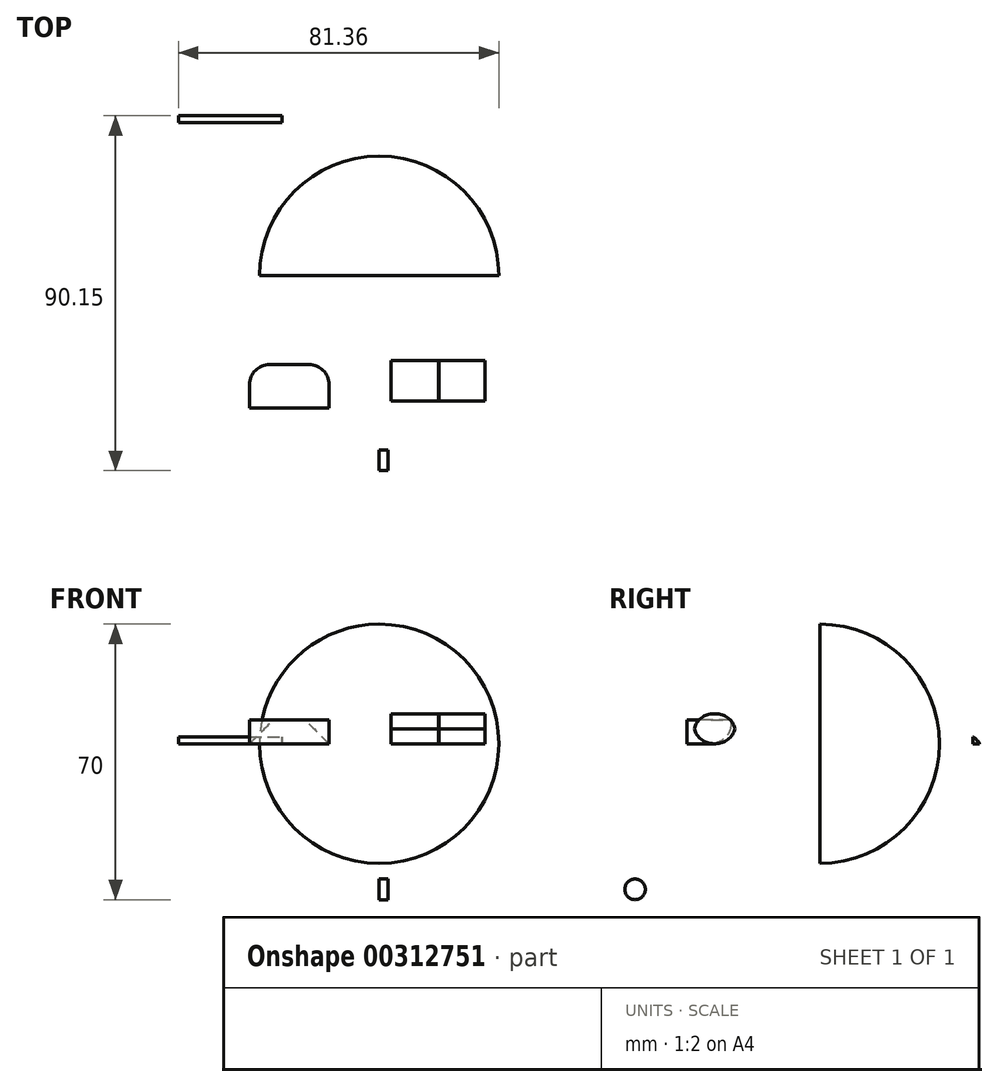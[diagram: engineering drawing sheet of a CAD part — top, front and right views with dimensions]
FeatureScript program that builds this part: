
annotation { "Feature Type Name" : "Feature", "Feature Type Description" : "" }
export const myFeature = defineFeature(function(context is Context, id is Id, definition is map)
    precondition{}
    {
        {
            var Q0;
            Q0=qCreatedBy(makeId("Front.planeOp"),FACE);
            var sketch = newSketch(context, id + "F0", { "sketchPlane" : qUnion([Q0])});
            skCircle(sketch, "E0", {"center": v(0, 0) * mm, "radius": 30.38 * mm});
            skLineSegment(sketch, "E1", {"start": v(0, 0) * mm, "end": v(30.38, 0) * mm});
            skLineSegment(sketch, "E2", {"start": v(30.38, 0) * mm, "end": v(-30.38, 0) * mm});
            skSolve(sketch);
        }
        {
            var Q0;
            {var subQ0=sQuery(id+"F0.wireOp",EDGE,"E2");var subQ4=makeQuery(id+"F0.imprint","IMPRINT",VERTEX,{"derivedFrom":subQ0});Q0=makeQuery(id+"F0.imprint","IMPRINT",FACE,{"disambiguationData":[TD([[makeQuery(id+"F0.imprint","IMPRINT",EDGE,{"disambiguationData":[TD([[subQ4,1.0]])],"derivedFrom":subQ0}),-1.0]])]});}
            var Q1;
            Q1=sQuery(id+"F0.wireOp",EDGE,"E2");
            revolve(context, id + "F1", {"entities" : qUnion([Q0]), "axis" : qUnion([Q1]), "revolveType" : RevolveType.ONE_DIRECTION, "angle" : 180 * degree});
        }
        {
            var Q0;
            Q0=qCreatedBy(makeId("Top.planeOp"),FACE);
            var sketch = newSketch(context, id + "F2", { "sketchPlane" : qUnion([Q0])});
            skLineSegment(sketch, "E3.bottom", {"start": v(26.83, -21.37) * mm, "end": v(15.2, -21.37) * mm});
            skLineSegment(sketch, "E3.top", {"start": v(26.83, -32.04) * mm, "end": v(15.2, -32.04) * mm});
            skLineSegment(sketch, "E3.left", {"start": v(26.83, -21.37) * mm, "end": v(26.83, -32.04) * mm});
            skLineSegment(sketch, "E3.right", {"start": v(15.2, -21.37) * mm, "end": v(15.2, -32.04) * mm});
            skLineSegment(sketch, "E4.bottom", {"start": v(15.04, -21.37) * mm, "end": v(2.99, -21.37) * mm});
            skLineSegment(sketch, "E4.top", {"start": v(15.04, -32.04) * mm, "end": v(2.99, -32.04) * mm});
            skLineSegment(sketch, "E4.left", {"start": v(15.04, -21.37) * mm, "end": v(15.04, -32.04) * mm});
            skLineSegment(sketch, "E4.right", {"start": v(2.99, -21.37) * mm, "end": v(2.99, -32.04) * mm});
            skSolve(sketch);
        }
        {
            var Q0;
            Q0 = qSketchRegion(id + "F2", true);
            extrude(context, id + "F3", {"entities" : qUnion([Q0]), "depth" : 7.62 * mm});
        }
        {
            var Q0;
            Q0=makeQuery(id+"F3.opExtrude","CAP_EDGE",EDGE,{"disambiguationData":[OSD([sQuery(id+"F2.wireOp",EDGE,"E3.bottom")])],"isStart":true});
            var Q1;
            Q1=makeQuery(id+"F3.opExtrude","CAP_EDGE",EDGE,{"disambiguationData":[OSD([sQuery(id+"F2.wireOp",EDGE,"E4.bottom")])],"isStart":true});
            var Q2;
            Q2=makeQuery(id+"F3.opExtrude","CAP_EDGE",EDGE,{"disambiguationData":[OSD([sQuery(id+"F2.wireOp",EDGE,"E4.top")])],"isStart":true});
            var Q3;
            Q3=makeQuery(id+"F3.opExtrude","CAP_EDGE",EDGE,{"disambiguationData":[OSD([sQuery(id+"F2.wireOp",EDGE,"E3.top")])],"isStart":true});
            var Q4;
            Q4=makeQuery(id+"F3.opExtrude","CAP_EDGE",EDGE,{"disambiguationData":[OSD([sQuery(id+"F2.wireOp",EDGE,"E4.top")])],"isStart":false});
            var Q5;
            Q5=makeQuery(id+"F3.opExtrude","CAP_EDGE",EDGE,{"disambiguationData":[OSD([sQuery(id+"F2.wireOp",EDGE,"E3.top")])],"isStart":false});
            var Q6;
            Q6=makeQuery(id+"F3.opExtrude","CAP_EDGE",EDGE,{"disambiguationData":[OSD([sQuery(id+"F2.wireOp",EDGE,"E4.bottom")])],"isStart":false});
            var Q7;
            Q7=makeQuery(id+"F3.opExtrude","CAP_EDGE",EDGE,{"disambiguationData":[OSD([sQuery(id+"F2.wireOp",EDGE,"E3.bottom")])],"isStart":false});
            fillet(context, id + "F4", {"entities" : qUnion([Q0, Q1, Q2, Q3, Q4, Q5, Q6, Q7]), "radius" : 5.08 * mm, "tangentPropagation" : true, "allowEdgeOverflow" : false});
        }
        {
            var Q0;
            Q0=qCreatedBy(makeId("Right.planeOp"),FACE);
            var sketch = newSketch(context, id + "F5", { "sketchPlane" : qUnion([Q0])});
            skCircle(sketch, "E5", {"center": v(-46.92, -37) * mm, "radius": 2.62 * mm});
            skSolve(sketch);
        }
        {
            var Q0;
            Q0 = qSketchRegion(id + "F5", true);
            extrude(context, id + "F6", {"entities" : qUnion([Q0]), "depth" : 2.3 * mm});
        }
        {
            var Q0;
            Q0=qCreatedBy(makeId("Top.planeOp"),FACE);
            var sketch = newSketch(context, id + "F7", { "sketchPlane" : qUnion([Q0])});
            skLineSegment(sketch, "E6.bottom", {"start": v(-32.94, -22.56) * mm, "end": v(-12.78, -22.56) * mm});
            skLineSegment(sketch, "E6.top", {"start": v(-32.94, -33.69) * mm, "end": v(-12.78, -33.69) * mm});
            skLineSegment(sketch, "E6.left", {"start": v(-32.94, -22.56) * mm, "end": v(-32.94, -33.69) * mm});
            skLineSegment(sketch, "E6.right", {"start": v(-12.78, -22.56) * mm, "end": v(-12.78, -33.69) * mm});
            skSolve(sketch);
        }
        {
            var Q0;
            Q0 = qSketchRegion(id + "F7", true);
            extrude(context, id + "F8", {"entities" : qUnion([Q0]), "depth" : 6.1 * mm});
        }
        {
            var Q0;
            Q0=makeQuery(id+"F8.opExtrude","SWEPT_EDGE",EDGE,{"disambiguationData":[OSD([sQuery(id+"F7.wireOp",EDGE,"E6.bottom"),sQuery(id+"F7.wireOp",EDGE,"E6.right")])]});
            var Q1;
            Q1=makeQuery(id+"F8.opExtrude","SWEPT_EDGE",EDGE,{"disambiguationData":[OSD([sQuery(id+"F7.wireOp",EDGE,"E6.bottom"),sQuery(id+"F7.wireOp",EDGE,"E6.left")])]});
            var Q2;
            Q2=makeQuery(id+"F8.opExtrude","CAP_EDGE",EDGE,{"disambiguationData":[OSD([sQuery(id+"F7.wireOp",EDGE,"E6.bottom")])],"isStart":true});
            fillet(context, id + "F9", {"entities" : qUnion([Q0, Q1, Q2]), "radius" : 5.08 * mm, "tangentPropagation" : true, "allowEdgeOverflow" : false});
        }
        {
            var Q0;
            Q0=qCreatedBy(makeId("Top.planeOp"),FACE);
            var sketch = newSketch(context, id + "F10", { "sketchPlane" : qUnion([Q0])});
            skLineSegment(sketch, "E7.bottom", {"start": v(-50.98, 40.6) * mm, "end": v(-24.7, 40.6) * mm});
            skLineSegment(sketch, "E7.top", {"start": v(-50.98, 38.87) * mm, "end": v(-24.7, 38.87) * mm});
            skLineSegment(sketch, "E7.left", {"start": v(-50.98, 40.6) * mm, "end": v(-50.98, 38.87) * mm});
            skLineSegment(sketch, "E7.right", {"start": v(-24.7, 40.6) * mm, "end": v(-24.7, 38.87) * mm});
            skSolve(sketch);
        }
        {
            var Q0;
            Q0 = qSketchRegion(id + "F10", true);
            extrude(context, id + "F11", {"entities" : qUnion([Q0]), "depth" : 2.54 * mm});
        }
        {
            var Q0;
            Q0=makeQuery(id+"F11.opExtrude","CAP_EDGE",EDGE,{"disambiguationData":[OSD([sQuery(id+"F10.wireOp",EDGE,"E7.bottom")])],"isStart":false});
            fillet(context, id + "F12", {"entities" : qUnion([Q0]), "radius" : 5.08 * mm, "tangentPropagation" : true, "allowEdgeOverflow" : false});
        }
    });
